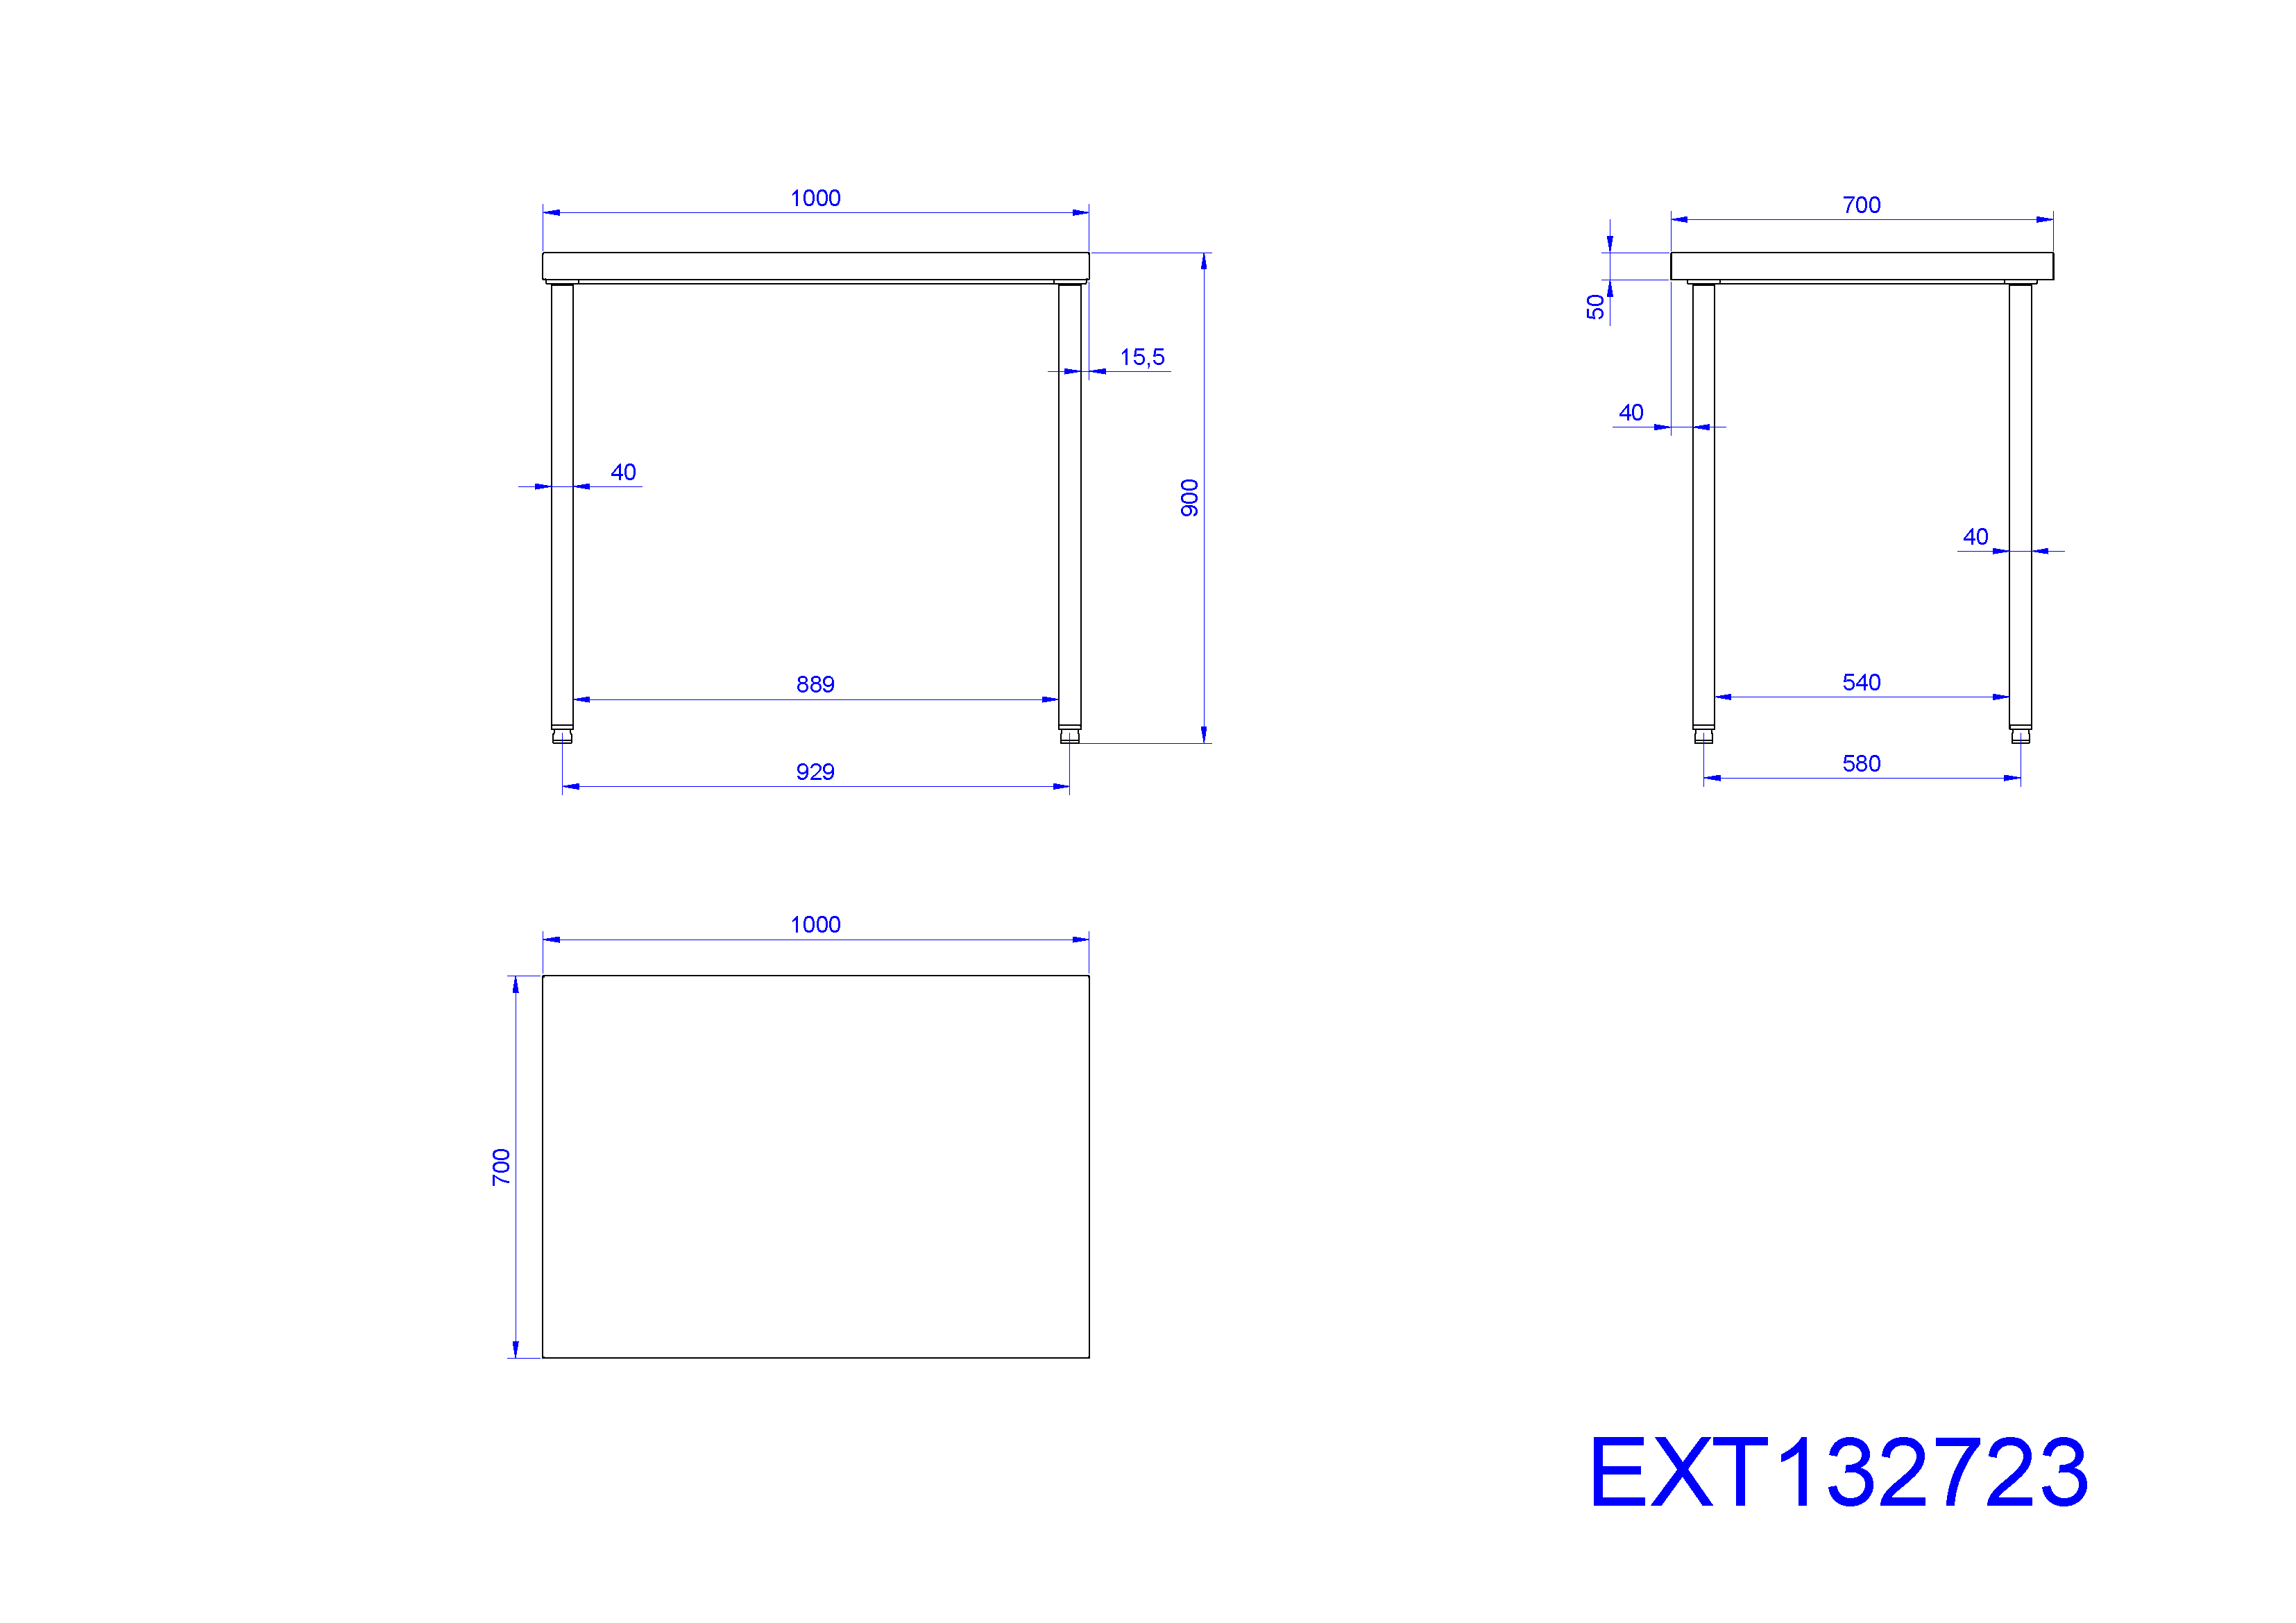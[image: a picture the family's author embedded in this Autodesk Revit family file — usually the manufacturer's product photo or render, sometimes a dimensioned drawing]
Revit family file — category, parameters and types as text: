
# Revit family: QF_ZANUSSI_132817_MLA716PN
name_source: partatom
category: Attrezzature speciali
units: mm (PartAtom-declared; Revit-internal decimal feet)

## family parameters
Basato su piano di lavoro = No
Condiviso = No
Punto di calcolo locali = No
Quota connettore circolare = Usa diametro
Sempre verticale = Sì
Taglio con vuoti quando caricato = No
Tipo di parte = Normale

## types (1)
- Standard
    Accessory = Sì
    Cold Water Size = 0 mm
    Compressed Air Pressure = 0.0 Pa
    Compressed Air Size = 0 mm
    Compressed Air Volume = 0.0 L/s
    Condensate Return Size = 0 mm
    Cycle = 0 Hz
    Depth Actual = 700 mm  [stored 2.29659 ft]
    Descrizione = CUPBOARD SINK 1 BOWL(500X500) 2 DOOR 700MM
    Direct Waste Size = 51 mm
    Gas Input Pressure = 0
    Gas KW = 0
    Gas Size = 0 mm
    HP = 0 HP
    Height Actual = 1000 mm  [stored 3.28084 ft]
    Hot Water Size = 0 mm
    Item Number = 132817
    Length Actual = 700 mm  [stored 2.29659 ft]
    Modello = MLA716PN
    Phase = 0
    Produttore = Zanussi
    Prospetto di default = 0 mm  [stored 0 ft]
    Refrigerant Compressor Remote = Sì
    Refrigeration Liquid Line Size = 0 mm  [stored 0 ft]
    Refrigeration Suction Line Size = 0 mm  [stored 0 ft]
    Steam Consumption per Hour = 0
    Steam Supply Maximum Pressure = 0.0 Pa
    Steam Supply Minimum Pressure = 0.0 Pa
    Steam Supply Size = 0 mm
    URL = http://www.zanussiprofessional.com
    URL Manufacturer = http://www.zanussiprofessional.com
    Volts = 0 V
    Watts = 0 W
    Weight = 40.00 kg

note: source unit labels omitted for Gas Input Pressure — the stored unit's dimension contradicts the parameter name (converter mislabeling)

note: [stored X ft] marks values corroborated as IEEE doubles in the binary element streams (Revit-internal decimal feet)

## geometry (parser evidence)
native form markers: Sweep x3
no freeform markers — native parametric forms only
